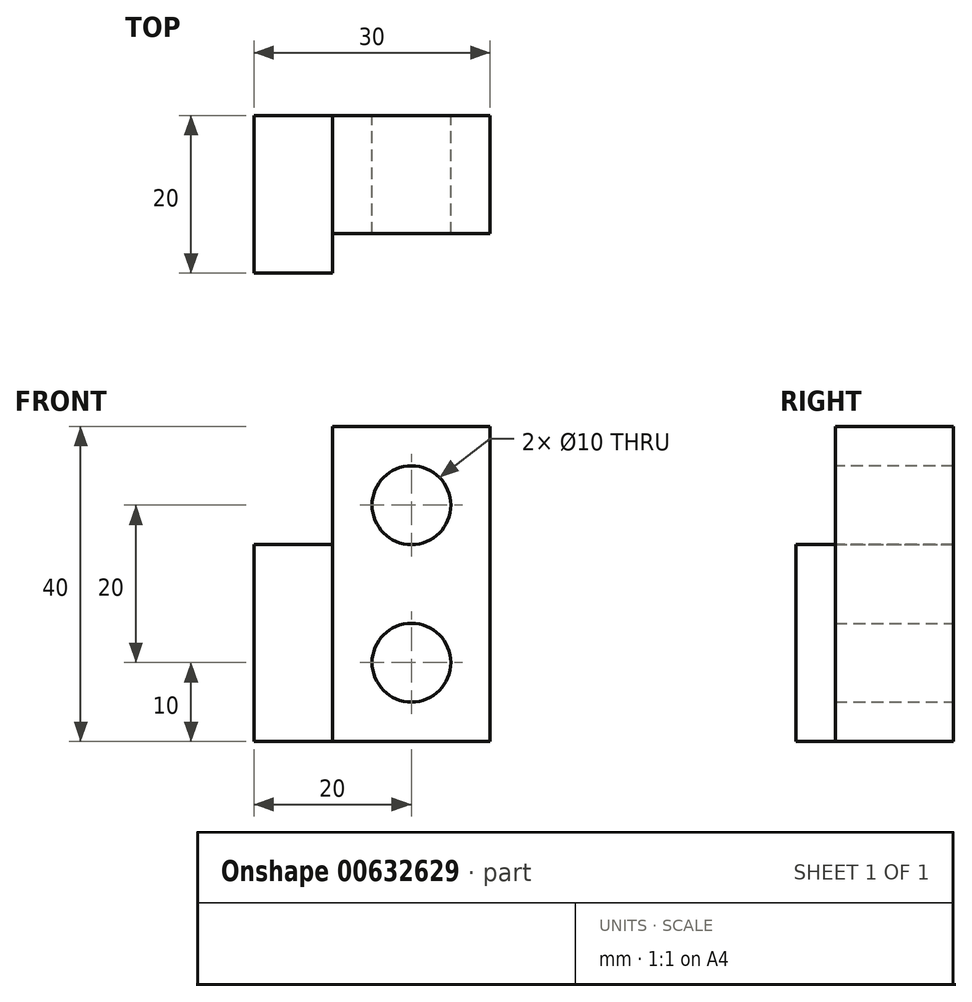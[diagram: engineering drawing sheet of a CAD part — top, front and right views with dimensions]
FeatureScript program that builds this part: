
annotation { "Feature Type Name" : "Feature", "Feature Type Description" : "" }
export const myFeature = defineFeature(function(context is Context, id is Id, definition is map)
    precondition{}
    {
        {
            var Q0;
            Q0=qCreatedBy(makeId("Front.planeOp"),FACE);
            var sketch = newSketch(context, id + "F0", { "sketchPlane" : qUnion([Q0])});
            skLineSegment(sketch, "E0.bottom", {"start": v(10, 20) * mm, "end": v(-10, 20) * mm});
            skLineSegment(sketch, "E0.top", {"start": v(10, -20) * mm, "end": v(-10, -20) * mm});
            skLineSegment(sketch, "E0.left", {"start": v(10, 20) * mm, "end": v(10, -20) * mm});
            skLineSegment(sketch, "E0.right", {"start": v(-10, 20) * mm, "end": v(-10, -20) * mm});
            skPoint(sketch, "E0.middle", {"position": v(0, 0) * mm});
            skLineSegment(sketch, "E1.bottom", {"start": v(-10, -20) * mm, "end": v(-20, -20) * mm});
            skLineSegment(sketch, "E1.top", {"start": v(-10, 5) * mm, "end": v(-20, 5) * mm});
            skLineSegment(sketch, "E1.left", {"start": v(-10, -20) * mm, "end": v(-10, 5) * mm});
            skLineSegment(sketch, "E1.right", {"start": v(-20, -20) * mm, "end": v(-20, 5) * mm});
            skCircle(sketch, "E2", {"center": v(0, -10) * mm, "radius": 5 * mm});
            skSolve(sketch);
        }
        {
            var Q0;
            Q0=makeQuery(id+"F0.imprint","IMPRINT",FACE,{"disambiguationData":[TD([[makeQuery(id+"F0.imprint","IMPRINT",EDGE,{"derivedFrom":sQuery(id+"F0.wireOp",EDGE,"E0.bottom")}),1.0]])]});
            extrude(context, id + "F1", {"entities" : qUnion([Q0]), "depth" : 15 * mm, "offsetDistance" : 25 * mm});
        }
        {
            var Q0;
            Q0=makeQuery(id+"F0.imprint","IMPRINT",FACE,{"disambiguationData":[TD([[makeQuery(id+"F0.imprint","IMPRINT",EDGE,{"derivedFrom":sQuery(id+"F0.wireOp",EDGE,"E1.bottom")}),-1.0]])]});
            extrude(context, id + "F2", {"entities" : qUnion([Q0]), "operationType" : NewBodyOperationType.ADD, "depth" : 20 * mm, "offsetDistance" : 25 * mm});
        }
        {
            var Q0;
            Q0=makeQuery(id+"F1.opExtrude","CAP_FACE",FACE,{"disambiguationData":[OSD([sQuery(id+"F0.wireOp",EDGE,"E0.bottom"),sQuery(id+"F0.wireOp",EDGE,"E0.top"),sQuery(id+"F0.wireOp",EDGE,"E0.left"),sQuery(id+"F0.wireOp",EDGE,"E0.right"),sQuery(id+"F0.wireOp",EDGE,"E1.left"),sQuery(id+"F0.wireOp",EDGE,"E2")])],"isStart":false});
            var sketch = newSketch(context, id + "F3", { "sketchPlane" : qUnion([Q0])});
            skCircle(sketch, "E3", {"center": v(0, 10) * mm, "radius": 5 * mm});
            skSolve(sketch);
        }
        {
            var Q0;
            Q0=makeQuery(id+"F3.imprint","IMPRINT",FACE,{"disambiguationData":[TD([[makeQuery(id+"F3.imprint","IMPRINT",EDGE,{"derivedFrom":sQuery(id+"F3.wireOp",EDGE,"E3")}),1.0]])]});
            var Q1;
            {var subQ0=sQuery(id+"F0.wireOp",EDGE,"E1.left");Q1=makeQuery(id+"F2.boolean.opBoolean","MERGE",FACE,{"derivedFrom":[makeQuery(id+"F1.opExtrude","CAP_FACE",FACE,{"disambiguationData":[OSD([sQuery(id+"F0.wireOp",EDGE,"E0.bottom"),sQuery(id+"F0.wireOp",EDGE,"E0.top"),sQuery(id+"F0.wireOp",EDGE,"E0.left"),sQuery(id+"F0.wireOp",EDGE,"E0.right"),subQ0,sQuery(id+"F0.wireOp",EDGE,"E2")])],"isStart":true}),makeQuery(id+"F2.opExtrude","CAP_FACE",FACE,{"disambiguationData":[OSD([sQuery(id+"F0.wireOp",EDGE,"E1.bottom"),sQuery(id+"F0.wireOp",EDGE,"E1.top"),subQ0,sQuery(id+"F0.wireOp",EDGE,"E1.right")])],"isStart":true})]});}
            extrude(context, id + "F4", {"entities" : qUnion([Q0]), "operationType" : NewBodyOperationType.REMOVE, "endBound" : BoundingType.UP_TO_SURFACE, "oppositeDirection" : true, "depth" : 25 * mm, "endBoundEntityFace" : qUnion([Q1]), "offsetDistance" : 25 * mm});
        }
    });
